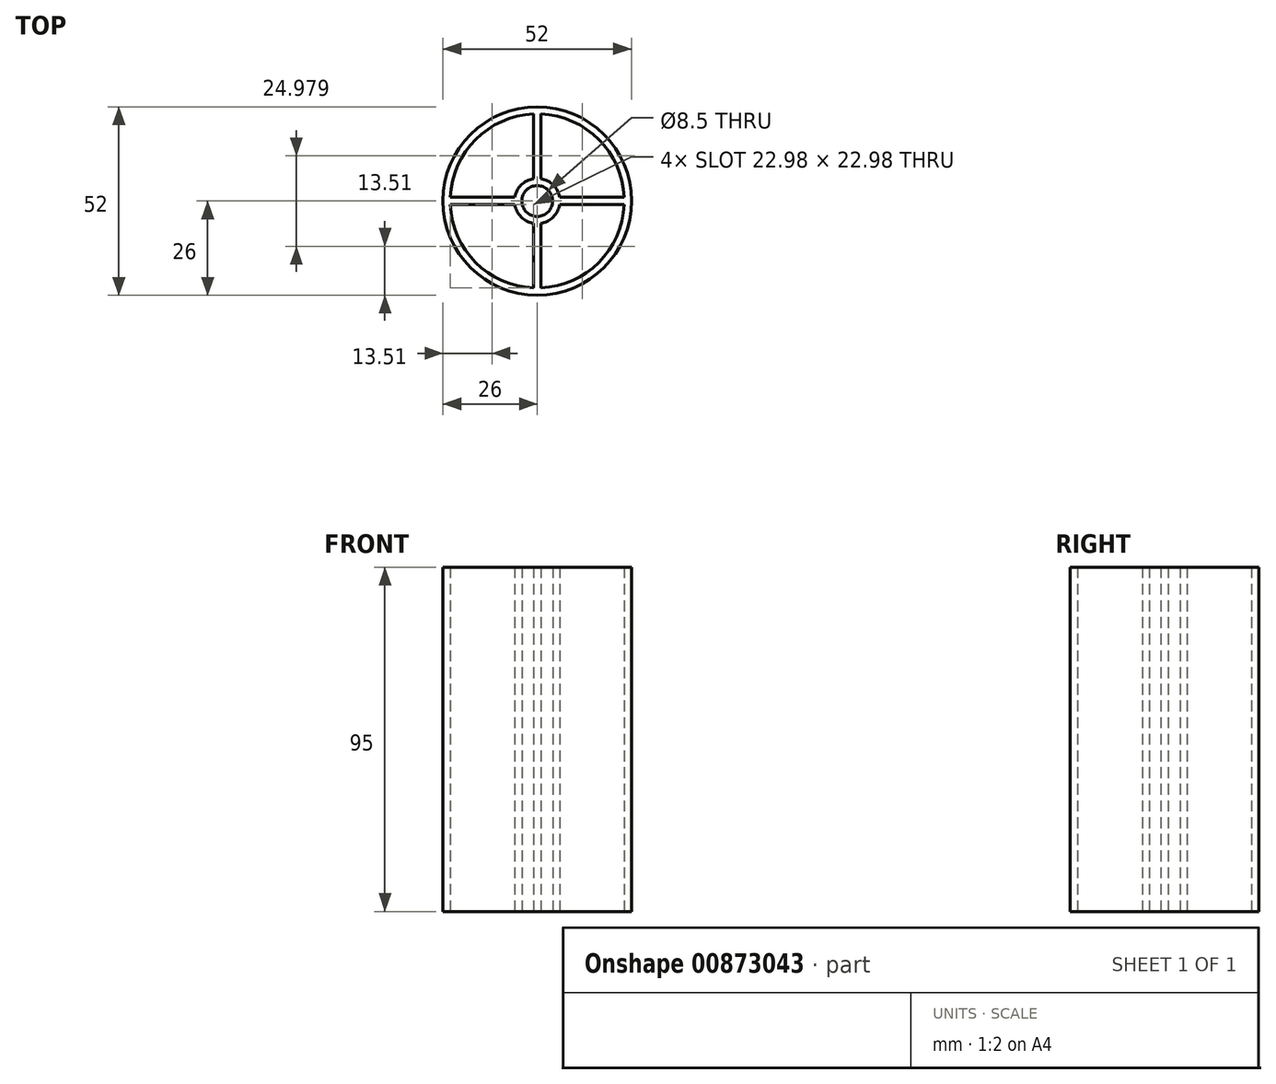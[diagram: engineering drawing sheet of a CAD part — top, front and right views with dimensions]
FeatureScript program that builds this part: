
annotation { "Feature Type Name" : "Feature", "Feature Type Description" : "" }
export const myFeature = defineFeature(function(context is Context, id is Id, definition is map)
    precondition{}
    {
        {
            var Q0;
            Q0=qCreatedBy(makeId("Top.planeOp"),FACE);
            var sketch = newSketch(context, id + "F0", { "sketchPlane" : qUnion([Q0])});
            skCircle(sketch, "E0", {"center": v(0, 0) * mm, "radius": 4.25 * mm});
            skCircle(sketch, "E1", {"center": v(0, 0) * mm, "radius": 26 * mm});
            skCircle(sketch, "E2", {"center": v(0, 0) * mm, "radius": 24 * mm});
            skCircle(sketch, "E3", {"center": v(0, 0) * mm, "radius": 6.25 * mm});
            skLineSegment(sketch, "E4.bottom", {"start": v(-1, 5) * mm, "end": v(1, 5) * mm});
            skLineSegment(sketch, "E4.top", {"start": v(-1, 25) * mm, "end": v(1, 25) * mm});
            skLineSegment(sketch, "E4.left", {"start": v(-1, 25) * mm, "end": v(-1, 5) * mm});
            skLineSegment(sketch, "E4.right", {"start": v(1, 25) * mm, "end": v(1, 5) * mm});
            skLineSegment(sketch, "E5.bottom", {"start": v(-1, -25) * mm, "end": v(1, -25) * mm});
            skLineSegment(sketch, "E5.top", {"start": v(-1, -5) * mm, "end": v(1, -5) * mm});
            skLineSegment(sketch, "E5.left", {"start": v(-1, -5) * mm, "end": v(-1, -25) * mm});
            skLineSegment(sketch, "E5.right", {"start": v(1, -5) * mm, "end": v(1, -25) * mm});
            skLineSegment(sketch, "E6.bottom", {"start": v(-25, 1) * mm, "end": v(-5, 1) * mm});
            skLineSegment(sketch, "E6.top", {"start": v(-25, -1) * mm, "end": v(-5, -1) * mm});
            skLineSegment(sketch, "E6.left", {"start": v(-5, 1) * mm, "end": v(-5, -1) * mm});
            skLineSegment(sketch, "E6.right", {"start": v(-25, 1) * mm, "end": v(-25, -1) * mm});
            skLineSegment(sketch, "E7.bottom", {"start": v(5, 1) * mm, "end": v(25, 1) * mm});
            skLineSegment(sketch, "E7.top", {"start": v(5, -1) * mm, "end": v(25, -1) * mm});
            skLineSegment(sketch, "E7.left", {"start": v(25, 1) * mm, "end": v(25, -1) * mm});
            skLineSegment(sketch, "E7.right", {"start": v(5, 1) * mm, "end": v(5, -1) * mm});
            skSolve(sketch);
        }
        {
            var Q0;
            Q0=makeQuery(id+"F0.imprint","IMPRINT",FACE,{"disambiguationData":[TD([[makeQuery(id+"F0.imprint","IMPRINT",EDGE,{"derivedFrom":sQuery(id+"F0.wireOp",EDGE,"E1")}),1.0]])]});
            var Q1;
            {var subQ5=sQuery(id+"F0.wireOp",EDGE,"E6.right");Q1=makeQuery(id+"F0.imprint","IMPRINT",FACE,{"disambiguationData":[TD([[makeQuery(id+"F0.imprint","IMPRINT",EDGE,{"derivedFrom":subQ5}),1.0]])]});}
            var Q2;
            {var subQ5=sQuery(id+"F0.wireOp",EDGE,"E5.bottom");Q2=makeQuery(id+"F0.imprint","IMPRINT",FACE,{"disambiguationData":[TD([[makeQuery(id+"F0.imprint","IMPRINT",EDGE,{"derivedFrom":subQ5}),1.0]])]});}
            var Q3;
            {var subQ0=sQuery(id+"F0.wireOp",EDGE,"E5.left");var subQ1=sQuery(id+"F0.wireOp",EDGE,"E2");var subQ2=makeQuery(id+"F0.imprint","INTERSECT",VERTEX,{"derivedFrom":[subQ1,subQ0]});Q3=makeQuery(id+"F0.imprint","IMPRINT",FACE,{"disambiguationData":[TD([[makeQuery(id+"F0.imprint","IMPRINT",EDGE,{"disambiguationData":[TD([[subQ2,-1.0]])],"derivedFrom":subQ1}),1.0]])]});}
            var Q4;
            {var subQ0=sQuery(id+"F0.wireOp",EDGE,"E6.bottom");var subQ1=sQuery(id+"F0.wireOp",EDGE,"E2");var subQ2=makeQuery(id+"F0.imprint","INTERSECT",VERTEX,{"derivedFrom":[subQ1,subQ0]});Q4=makeQuery(id+"F0.imprint","IMPRINT",FACE,{"disambiguationData":[TD([[makeQuery(id+"F0.imprint","IMPRINT",EDGE,{"disambiguationData":[TD([[subQ2,-1.0]])],"derivedFrom":subQ1}),1.0]])]});}
            var Q5;
            {var subQ5=sQuery(id+"F0.wireOp",EDGE,"E6.left");Q5=makeQuery(id+"F0.imprint","IMPRINT",FACE,{"disambiguationData":[TD([[makeQuery(id+"F0.imprint","IMPRINT",EDGE,{"derivedFrom":subQ5}),-1.0]])]});}
            var Q6;
            {var subQ0=sQuery(id+"F0.wireOp",EDGE,"E7.bottom");var subQ1=sQuery(id+"F0.wireOp",EDGE,"E2");var subQ2=makeQuery(id+"F0.imprint","INTERSECT",VERTEX,{"derivedFrom":[subQ1,subQ0]});Q6=makeQuery(id+"F0.imprint","IMPRINT",FACE,{"disambiguationData":[TD([[makeQuery(id+"F0.imprint","IMPRINT",EDGE,{"disambiguationData":[TD([[subQ2,1.0]])],"derivedFrom":subQ1}),1.0]])]});}
            var Q7;
            {var subQ5=sQuery(id+"F0.wireOp",EDGE,"E7.left");Q7=makeQuery(id+"F0.imprint","IMPRINT",FACE,{"disambiguationData":[TD([[makeQuery(id+"F0.imprint","IMPRINT",EDGE,{"derivedFrom":subQ5}),-1.0]])]});}
            var Q8;
            {var subQ0=sQuery(id+"F0.wireOp",EDGE,"E4.right");var subQ1=sQuery(id+"F0.wireOp",EDGE,"E2");var subQ2=makeQuery(id+"F0.imprint","INTERSECT",VERTEX,{"derivedFrom":[subQ1,subQ0]});Q8=makeQuery(id+"F0.imprint","IMPRINT",FACE,{"disambiguationData":[TD([[makeQuery(id+"F0.imprint","IMPRINT",EDGE,{"disambiguationData":[TD([[subQ2,-1.0]])],"derivedFrom":subQ1}),1.0]])]});}
            var Q9;
            {var subQ5=sQuery(id+"F0.wireOp",EDGE,"E4.top");Q9=makeQuery(id+"F0.imprint","IMPRINT",FACE,{"disambiguationData":[TD([[makeQuery(id+"F0.imprint","IMPRINT",EDGE,{"derivedFrom":subQ5}),-1.0]])]});}
            var Q10;
            {var subQ5=sQuery(id+"F0.wireOp",EDGE,"E4.bottom");Q10=makeQuery(id+"F0.imprint","IMPRINT",FACE,{"disambiguationData":[TD([[makeQuery(id+"F0.imprint","IMPRINT",EDGE,{"derivedFrom":subQ5}),1.0]])]});}
            var Q11;
            {var subQ5=sQuery(id+"F0.wireOp",EDGE,"E7.right");Q11=makeQuery(id+"F0.imprint","IMPRINT",FACE,{"disambiguationData":[TD([[makeQuery(id+"F0.imprint","IMPRINT",EDGE,{"derivedFrom":subQ5}),1.0]])]});}
            var Q12;
            Q12=makeQuery(id+"F0.imprint","IMPRINT",FACE,{"disambiguationData":[TD([[makeQuery(id+"F0.imprint","IMPRINT",EDGE,{"derivedFrom":sQuery(id+"F0.wireOp",EDGE,"E0")}),-1.0]])]});
            var Q13;
            {var subQ5=sQuery(id+"F0.wireOp",EDGE,"E5.top");Q13=makeQuery(id+"F0.imprint","IMPRINT",FACE,{"disambiguationData":[TD([[makeQuery(id+"F0.imprint","IMPRINT",EDGE,{"derivedFrom":subQ5}),-1.0]])]});}
            extrude(context, id + "F1", {"entities" : qUnion([Q0, Q1, Q2, Q3, Q4, Q5, Q6, Q7, Q8, Q9, Q10, Q11, Q12, Q13]), "depth" : 95 * mm, "offsetDistance" : 25.4 * mm});
        }
    });
